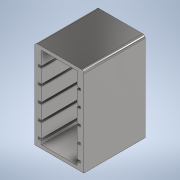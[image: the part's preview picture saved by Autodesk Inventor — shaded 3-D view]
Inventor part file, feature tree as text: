
AUTODESK INVENTOR PART (.ipt)
format: ipt  version: 2021 (Build 250183000, 183)  size: 185,856 bytes
history: native  units: mm
features: sketch x4, extrude x2, fillet x1, hole x1
ambient origin geometry x8: Origin, YZ Plane, XZ Plane, XY Plane, X Axis, Y Axis, Z Axis, Center Point
bodies: Solid1 (feature_tree)
feature tree (8):
  extrude  "Extrusion1"  Depth=130.0mm
  extrude  "Extrusion2"  Depth=20.0mm
  fillet  "Fillet1"  Radius=5.0mm
  hole  "Hole1"  [1 undecoded]
  sketch  "Sketch4"  dims[d11=5.0mm d12=3.0mm d13=20.0mm d14=3.0mm d15=20.0mm d16=5.0mm d17=3.0mm d18=20.0mm d19=3.0mm d20=3.0mm d21=90.0mm d22=0.0mm d23=4.0mm d24=3.0mm d25=5.0mm d26=5.0mm d27=3.0mm d28=5.0mm d29=5.0mm d30=2.6416mm d31=7.01mm d32=4.0mm d33=2.0mm d34=90.0deg d35=10.979mm d36=0.0mm]
  sketch  "Sketch1"  dims[d0=72.0mm d1=130.0mm]
  sketch  "Sketch2"  dims[d5=90.0mm d6=0.0mm d7=20.0mm d8=5.0mm]
  sketch  "Sketch3"  dims[d9=3.0mm d10=20.0mm]
note: 1 required parameter value undecoded (feature->parameter linkage not recoverable at this tier; creation-order binding heuristic only, values carry confidence <= 0.55)
